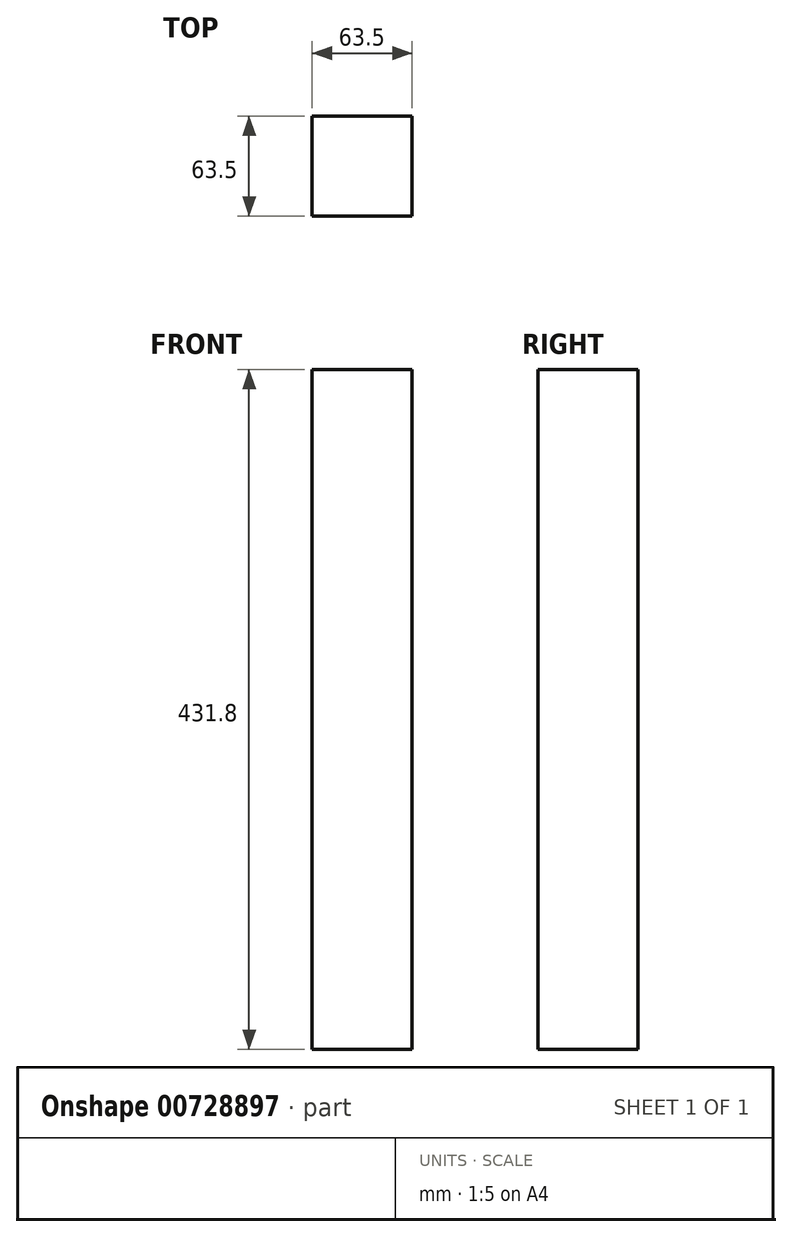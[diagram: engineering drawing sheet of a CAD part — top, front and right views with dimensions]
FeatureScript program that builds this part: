
annotation { "Feature Type Name" : "Feature", "Feature Type Description" : "" }
export const myFeature = defineFeature(function(context is Context, id is Id, definition is map)
    precondition{}
    {
        {
            var Q0;
            Q0=qCreatedBy(makeId("Top.planeOp"),FACE);
            var sketch = newSketch(context, id + "F0", { "sketchPlane" : qUnion([Q0])});
            skLineSegment(sketch, "E0.bottom", {"start": v(31.75, 31.75) * mm, "end": v(-31.75, 31.75) * mm});
            skLineSegment(sketch, "E0.top", {"start": v(31.75, -31.75) * mm, "end": v(-31.75, -31.75) * mm});
            skLineSegment(sketch, "E0.left", {"start": v(31.75, 31.75) * mm, "end": v(31.75, -31.75) * mm});
            skLineSegment(sketch, "E0.right", {"start": v(-31.75, 31.75) * mm, "end": v(-31.75, -31.75) * mm});
            skPoint(sketch, "E0.middle", {"position": v(0, 0) * mm});
            skSolve(sketch);
        }
        {
            var Q0;
            Q0=makeQuery(id+"F0.imprint","IMPRINT",FACE,{"disambiguationData":[TD([[makeQuery(id+"F0.imprint","IMPRINT",EDGE,{"derivedFrom":sQuery(id+"F0.wireOp",EDGE,"E0.bottom")}),1.0]])]});
            extrude(context, id + "F1", {"entities" : qUnion([Q0]), "oppositeDirection" : true, "depth" : 431.8 * mm, "offsetDistance" : 25.4 * mm});
        }
    });
